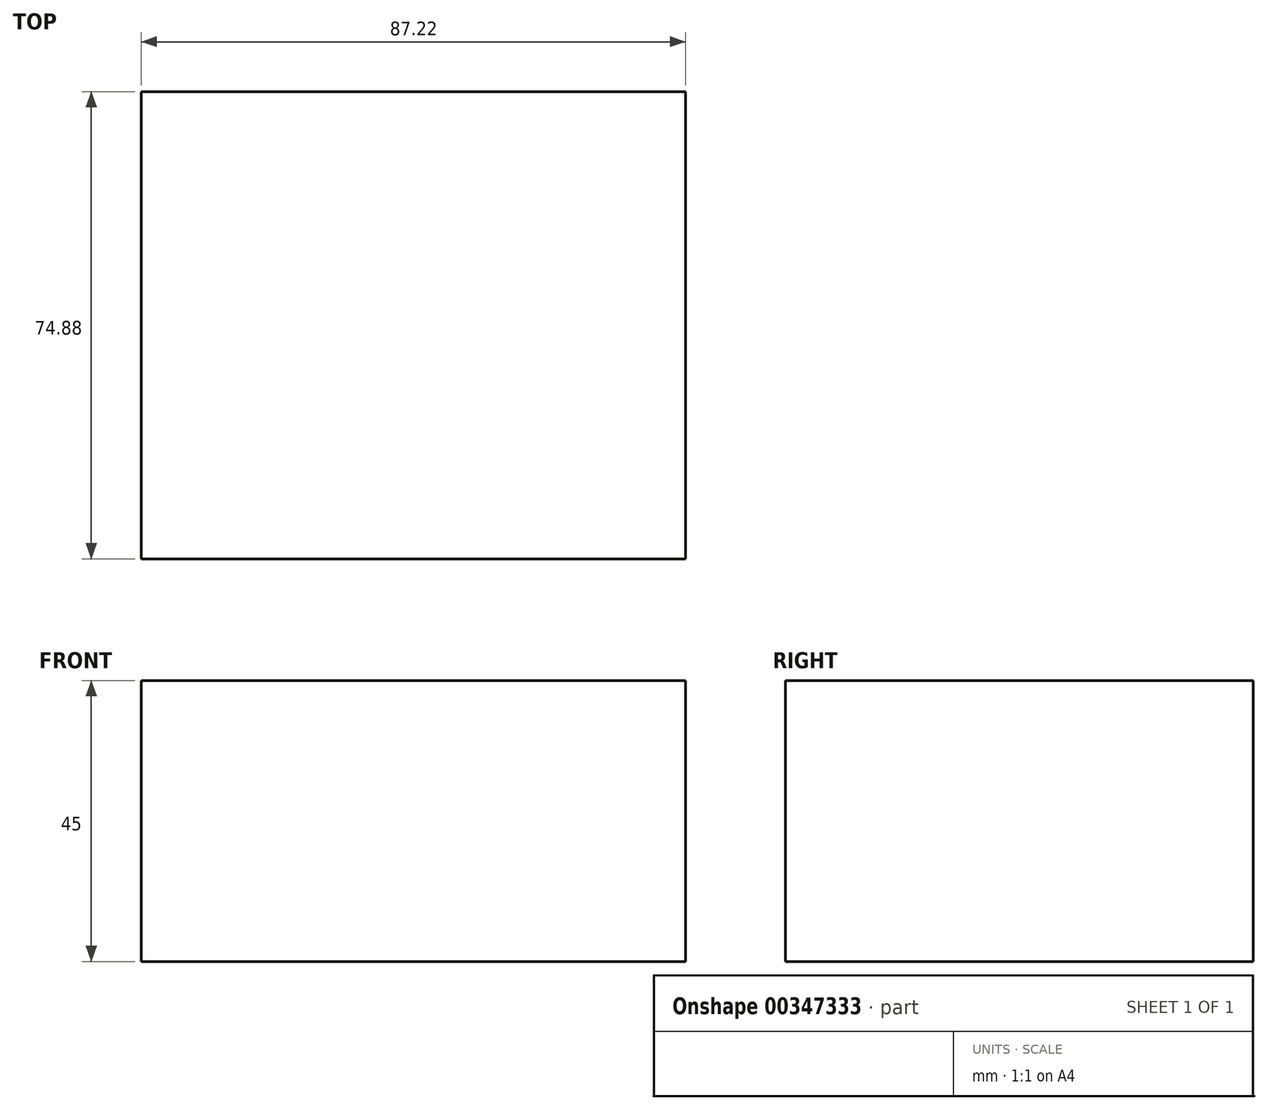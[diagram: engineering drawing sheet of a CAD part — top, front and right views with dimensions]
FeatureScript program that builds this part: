
annotation { "Feature Type Name" : "Feature", "Feature Type Description" : "" }
export const myFeature = defineFeature(function(context is Context, id is Id, definition is map)
    precondition{}
    {
        {
            var Q0;
            Q0=qCreatedBy(makeId("Top.planeOp"),FACE);
            var sketch = newSketch(context, id + "F0", { "sketchPlane" : qUnion([Q0])});
            skLineSegment(sketch, "E0.bottom", {"start": v(-43.6, 37.44) * mm, "end": v(43.6, 37.44) * mm});
            skLineSegment(sketch, "E0.top", {"start": v(-43.6, -37.44) * mm, "end": v(43.6, -37.44) * mm});
            skLineSegment(sketch, "E0.left", {"start": v(-43.6, 37.44) * mm, "end": v(-43.6, -37.44) * mm});
            skLineSegment(sketch, "E0.right", {"start": v(43.6, 37.44) * mm, "end": v(43.6, -37.44) * mm});
            skPoint(sketch, "E0.middle", {"position": v(0, 0) * mm});
            skSolve(sketch);
        }
        {
            var Q0;
            Q0 = qSketchRegion(id + "F0", true);
            extrude(context, id + "F1", {"entities" : qUnion([Q0]), "depth" : 45 * mm});
        }
    });
